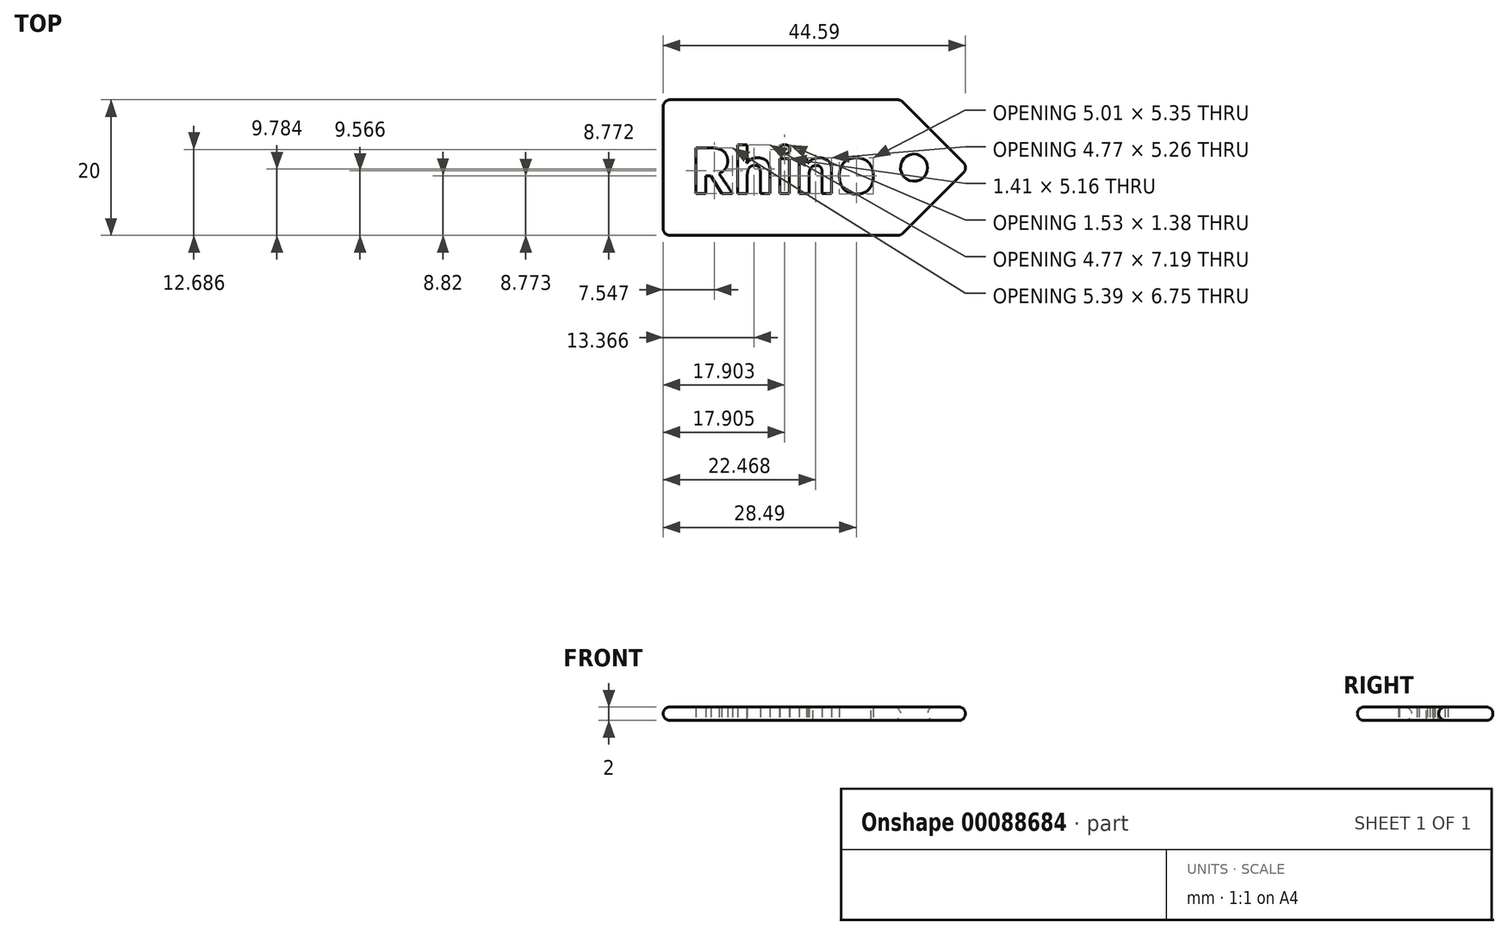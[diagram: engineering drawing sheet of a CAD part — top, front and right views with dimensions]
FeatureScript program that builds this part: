
annotation { "Feature Type Name" : "Feature", "Feature Type Description" : "" }
export const myFeature = defineFeature(function(context is Context, id is Id, definition is map)
    precondition{}
    {
        {
            var Q0;
            Q0=qCreatedBy(makeId("Top.planeOp"),FACE);
            var sketch = newSketch(context, id + "F0", { "sketchPlane" : qUnion([Q0])});
            skLineSegment(sketch, "E0.bottom", {"start": v(-17.5, 20) * mm, "end": v(17.5, 20) * mm});
            skLineSegment(sketch, "E0.top", {"start": v(-17.5, 0) * mm, "end": v(17.5, 0) * mm});
            skLineSegment(sketch, "E0.left", {"start": v(-17.5, 20) * mm, "end": v(-17.5, 0) * mm});
            skLineSegment(sketch, "E0.right", {"start": v(17.5, 20) * mm, "end": v(17.5, 0) * mm});
            skPoint(sketch, "E1.endSnap0", {"position": v(0, 20) * mm});
            skText(sketch, "E2", { "text": "Rhino", "fontName": "OpenSans-Bold.ttf"});
            skLineSegment(sketch, "E3", {"start": v(17.5, 20) * mm, "end": v(27.5, 10) * mm});
            skPoint(sketch, "E3.endSnap0", {"position": v(17.5, 10) * mm});
            skLineSegment(sketch, "E4", {"start": v(27.5, 10) * mm, "end": v(17.5, 0) * mm});
            skCircle(sketch, "E5", {"center": v(19.5, 10) * mm, "radius": 2 * mm});
            const initialGuessF0  = {"E2": [-0.0135, 0.00619, 1, 0, 0.00681]};
            skSetInitialGuess(sketch, initialGuessF0);
            skSolve(sketch);
        }
        {
            var Q0;
            Q0=makeQuery(id+"F0.imprint","IMPRINT",FACE,{"disambiguationData":[TD([[makeQuery(id+"F0.imprint","IMPRINT",EDGE,{"derivedFrom":sQuery(id+"F0.wireOp",EDGE,"E0.bottom")}),-1.0]])]});
            var Q1;
            Q1=makeQuery(id+"F0.imprint","IMPRINT",FACE,{"disambiguationData":[TD([[makeQuery(id+"F0.imprint","IMPRINT",EDGE,{"derivedFrom":sQuery(id+"F0.wireOp",EDGE,"E0.right")}),1.0]])]});
            extrude(context, id + "F1", {"entities" : qUnion([Q0, Q1]), "depth" : 2 * mm});
        }
        {
            var Q0;
            Q0=makeQuery(id+"F1.opExtrude","CAP_EDGE",EDGE,{"disambiguationData":[OSD([sQuery(id+"F0.wireOp",EDGE,"E0.bottom")])],"isStart":false});
            var Q1;
            Q1=makeQuery(id+"F1.opExtrude","CAP_EDGE",EDGE,{"disambiguationData":[OSD([sQuery(id+"F0.wireOp",EDGE,"E3")])],"isStart":false});
            var Q2;
            Q2=makeQuery(id+"F1.opExtrude","CAP_EDGE",EDGE,{"disambiguationData":[OSD([sQuery(id+"F0.wireOp",EDGE,"E4")])],"isStart":false});
            var Q3;
            Q3=makeQuery(id+"F1.opExtrude","CAP_EDGE",EDGE,{"disambiguationData":[OSD([sQuery(id+"F0.wireOp",EDGE,"E4")])],"isStart":true});
            var Q4;
            Q4=makeQuery(id+"F1.opExtrude","CAP_EDGE",EDGE,{"disambiguationData":[OSD([sQuery(id+"F0.wireOp",EDGE,"E3")])],"isStart":true});
            var Q5;
            Q5=makeQuery(id+"F1.opExtrude","CAP_EDGE",EDGE,{"disambiguationData":[OSD([sQuery(id+"F0.wireOp",EDGE,"E0.top")])],"isStart":false});
            var Q6;
            Q6=makeQuery(id+"F1.opExtrude","CAP_EDGE",EDGE,{"disambiguationData":[OSD([sQuery(id+"F0.wireOp",EDGE,"E0.top")])],"isStart":true});
            var Q7;
            Q7=makeQuery(id+"F1.opExtrude","SWEPT_EDGE",EDGE,{"disambiguationData":[OSD([sQuery(id+"F0.wireOp",EDGE,"E0.top"),sQuery(id+"F0.wireOp",EDGE,"E0.right"),sQuery(id+"F0.wireOp",EDGE,"E4")])]});
            var Q8;
            Q8=makeQuery(id+"F1.opExtrude","SWEPT_EDGE",EDGE,{"disambiguationData":[OSD([sQuery(id+"F0.wireOp",EDGE,"E0.top"),sQuery(id+"F0.wireOp",EDGE,"E0.left")])]});
            var Q9;
            Q9=makeQuery(id+"F1.opExtrude","CAP_EDGE",EDGE,{"disambiguationData":[OSD([sQuery(id+"F0.wireOp",EDGE,"E0.left")])],"isStart":false});
            var Q10;
            Q10=makeQuery(id+"F1.opExtrude","CAP_EDGE",EDGE,{"disambiguationData":[OSD([sQuery(id+"F0.wireOp",EDGE,"E0.left")])],"isStart":true});
            var Q11;
            Q11=makeQuery(id+"F1.opExtrude","SWEPT_EDGE",EDGE,{"disambiguationData":[OSD([sQuery(id+"F0.wireOp",EDGE,"E0.bottom"),sQuery(id+"F0.wireOp",EDGE,"E0.left")])]});
            var Q12;
            Q12=makeQuery(id+"F1.opExtrude","CAP_EDGE",EDGE,{"disambiguationData":[OSD([sQuery(id+"F0.wireOp",EDGE,"E0.bottom")])],"isStart":true});
            var Q13;
            Q13=makeQuery(id+"F1.opExtrude","SWEPT_EDGE",EDGE,{"disambiguationData":[OSD([sQuery(id+"F0.wireOp",EDGE,"E0.bottom"),sQuery(id+"F0.wireOp",EDGE,"E0.right"),sQuery(id+"F0.wireOp",EDGE,"E3")])]});
            fillet(context, id + "F2", {"entities" : qUnion([Q0, Q1, Q2, Q3, Q4, Q5, Q6, Q7, Q8, Q9, Q10, Q11, Q12, Q13]), "radius" : 1 * mm, "tangentPropagation" : true, "allowEdgeOverflow" : false});
        }
        {
            var Q0;
            Q0=makeQuery(id+"F2.opFillet","BLEND_EDGE",EDGE,{"blendedFrom":[makeQuery(id+"F1.opExtrude","CAP_EDGE",EDGE,{"disambiguationData":[OSD([sQuery(id+"F0.wireOp",EDGE,"E3")])],"isStart":true}),makeQuery(id+"F1.opExtrude","CAP_EDGE",EDGE,{"disambiguationData":[OSD([sQuery(id+"F0.wireOp",EDGE,"E4")])],"isStart":true})],"blendedInto":[]});
            var Q1;
            Q1=makeQuery(id+"F2.opFillet","BLEND_EDGE",EDGE,{"blendedFrom":[makeQuery(id+"F1.opExtrude","CAP_EDGE",EDGE,{"disambiguationData":[OSD([sQuery(id+"F0.wireOp",EDGE,"E3")])],"isStart":false}),makeQuery(id+"F1.opExtrude","CAP_EDGE",EDGE,{"disambiguationData":[OSD([sQuery(id+"F0.wireOp",EDGE,"E4")])],"isStart":false})],"blendedInto":[]});
            fillet(context, id + "F3", {"entities" : qUnion([Q0, Q1]), "radius" : 1 * mm, "tangentPropagation" : true, "allowEdgeOverflow" : false});
        }
        {
            var Q0;
            Q0=makeQuery(id+"F1.opExtrude","CAP_EDGE",EDGE,{"disambiguationData":[OSD([sQuery(id+"F0.wireOp",EDGE,"E5")])],"isStart":false});
            var Q1;
            Q1=makeQuery(id+"F1.opExtrude","CAP_EDGE",EDGE,{"disambiguationData":[OSD([sQuery(id+"F0.wireOp",EDGE,"E5")])],"isStart":true});
            fillet(context, id + "F4", {"entities" : qUnion([Q0, Q1]), "radius" : 1 * mm, "tangentPropagation" : true, "allowEdgeOverflow" : false});
        }
    });
